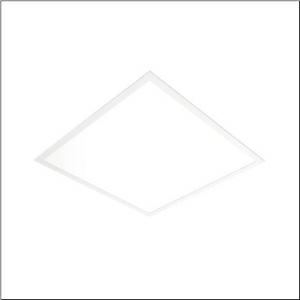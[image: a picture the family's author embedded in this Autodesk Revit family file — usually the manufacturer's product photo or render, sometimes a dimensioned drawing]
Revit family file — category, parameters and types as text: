
# Revit family: apollon_r__41_51mh12wd2443_fb74
name_source: partatom
category: Lighting Fixtures
units: mm (PartAtom-declared; Revit-internal decimal feet)

## family parameters
Cut with Voids When Loaded = No
Host = Face
Light Source = No
Part Type = Normal
Room Calculation Point = No
Round Connector Dimension = Use Diameter
Shared = No

## types (1)
- Apollon® 41 (1 x LED, 3500 lm, 28.5 W, 4000K)
    Apparent Load = 29 VA
    CIE Flux Codes = 61 87 97 100 100
    Color Rendering = 80
    Color Temperature = 4000K
    Default Elevation = 1800 mm
    Description = Apollon® 41, office luminaire, primary optical cover: prismatic diffuser, of PS, light emission: direct distribution, primary light characteristic: symmetric, installation type: lay-in mounting, LED, rated luminous flux: 3.500lm, luminous efficacy: 123lm/W, light colour: 840, colour temperature: 4000K, control gear: DALI 2, with terminal, 5-pole, mains connection: 220..240V, AC, 50/60Hz, suitable for self-contained emergency lighting element 58DB00B013A with integrated self-test function according to EN 60598-2-22, housing, of aluminium section, traffic white (RAL 9016), module: M600, length: 595mm, width: 595mm, height: 60mm, recess depth: 180mm, housing upper side, of sheet steel, protection rating (complete): IP20, protection rating (lamp compartment, on room side): IP40, insulation class (complete): insulation class II (safety insulation), certification: CE, ENEC, impact resistance: IK03, permissible operating ambient temperature: -25..+40°C, packaging unit: 1 piece
    Height = 0 mm  [stored 0 ft]
    Lamp = 1 x LED
    Lamp Light Flux = 3500 lm
    Lamp Power = 28.5 W
    Lamp count = 1
    Length = 600 mm
    Luminous efficacy = 123 lm/W
    Manufacturer = Siteco
    ModVariant = No
    Model = 51MH12WD2443
    Mounting Place = Ceiling
    Mounting Type = Recessed
    Number of Poles = 1
    OnlyDefault = Yes
    Power Factor = 1
    Product Name = Apollon® 41
    Product group = office luminaire | ceiling recessed
    ProductGroupID = 400
    Protection Class = Protection class II
    Protection Degree = IP 20
    RLX_Detail_Level = 1
    RLX_Emergency_Light_Flux = 0 lm
    RLX_Emergency_Type = 0
    RLX_Emergency_Type_DB = No
    RlxData = <blob elided: 12425 chars, md5=95cf8a8c>
    Socket = socket
    Standby Power = 0 W
    System Light Flux = 3500 lm
    System Power = 29 W
    Type Comments = Product without accessories
    Type Image = l_1291024.jpg
    URL = http://relux.com
    VarID = ---
    Voltage = 0 V
    Weight = 0.00 kg
    Width = 600 mm

note: [stored X ft] marks values corroborated as IEEE doubles in the binary element streams (Revit-internal decimal feet)

## geometry (parser evidence)
native form markers: Sweep x9
no freeform markers — native parametric forms only
